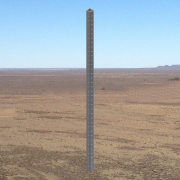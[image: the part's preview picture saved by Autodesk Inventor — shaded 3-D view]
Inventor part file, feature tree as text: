
AUTODESK INVENTOR PART (.ipt)
format: ipt  version: 2014 SP1 (Build 180222100, 222)  size: 273,920 bytes
history: native  units: in
note: dims shown in document units (in); Inventor stores cm internally (conversion verified against a paired STEP export)
features: sketch x3, hole x2, pattern_linear x2, extrude x1
ambient origin geometry x8: Origin, YZ Plane, XZ Plane, XY Plane, X Axis, Y Axis, Z Axis, Center Point
bodies: Solid1 (feature_tree)
feature tree (8):
  extrude  "Extrusion1"  Depth=1.0in
  hole  "Hole1"  [1 undecoded]
  pattern_linear  "Rectangular Pattern1"  Spacing1=1.0in  [1 undecoded]
  hole  "Hole2"  [1 undecoded]
  pattern_linear  "Rectangular Pattern2"  Spacing1=1.0in  [1 undecoded]
  sketch  "Sketch1"  dims[d0=1.0in d1=1.0in]
  sketch  "Sketch2"  dims[d2=0.125in d3=36.0in d4=0.0in]
  sketch  "Sketch3"  dims[d5=0.25in d6=1.0in d7=0.25in d8=0.75in d9=0.375in d10=0.25in d11=0.5635in d12=1.0in d13=0.8108in d14=13.7795in d16=1.0in d17=1.0in d18=0.25in d19=0.75in d20=0.375in d21=0.25in d22=0.5635in d23=1.0in d24=0.8108in d25=13.7795in d27=1.0in d28=0.125in d29=0.125in]
note: 4 required parameter values undecoded (feature->parameter linkage not recoverable at this tier; creation-order binding heuristic only, values carry confidence <= 0.55)
